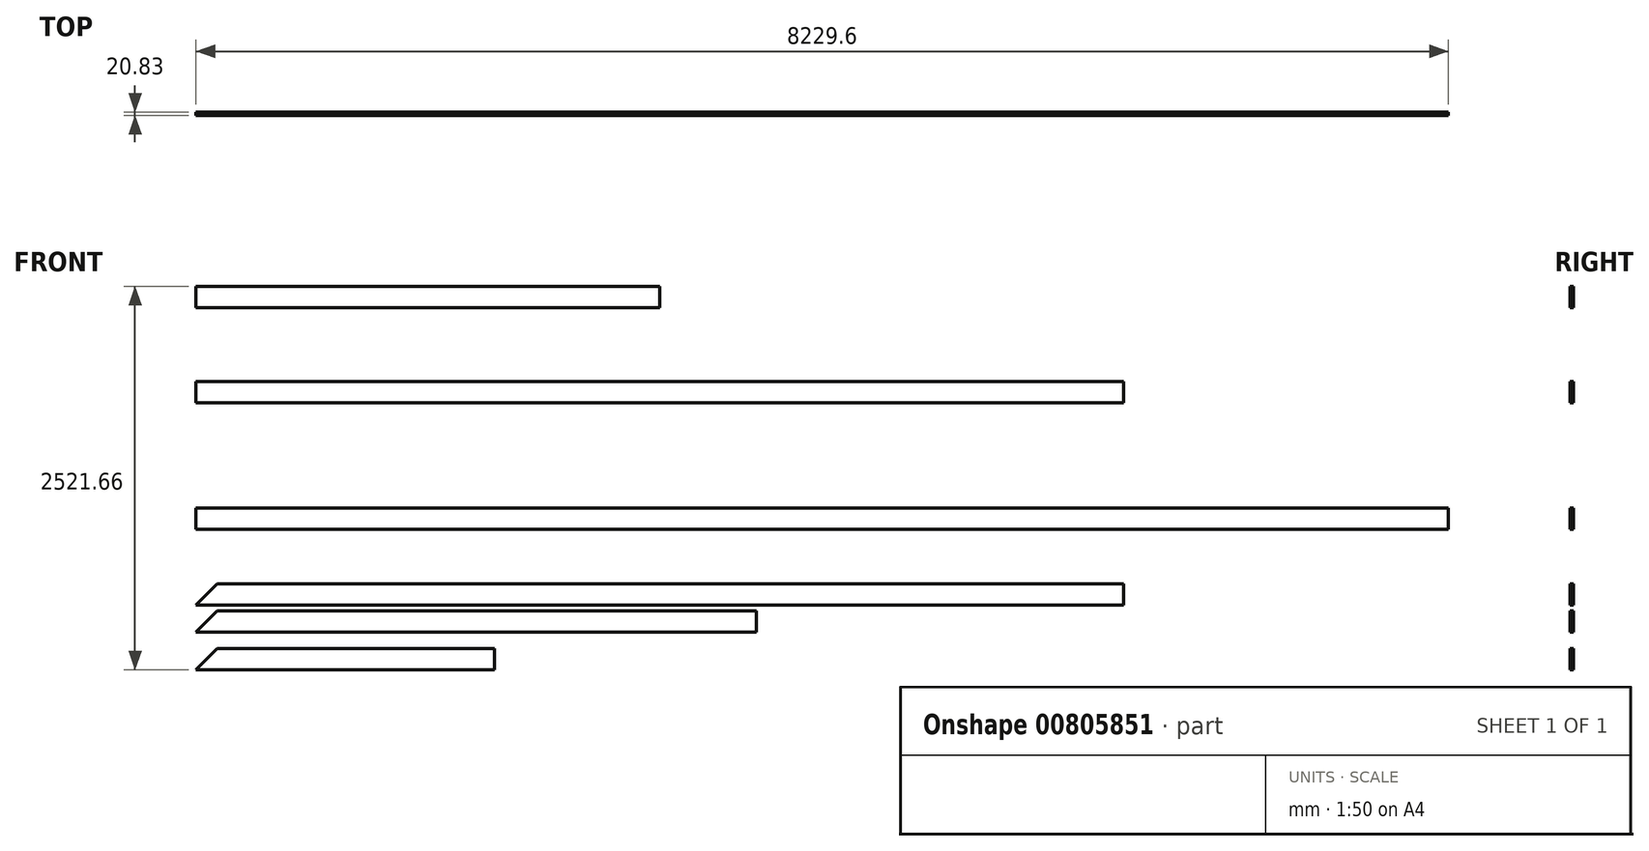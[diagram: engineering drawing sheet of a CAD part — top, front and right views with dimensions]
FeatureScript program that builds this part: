
annotation { "Feature Type Name" : "Feature", "Feature Type Description" : "" }
export const myFeature = defineFeature(function(context is Context, id is Id, definition is map)
    precondition{}
    {
        {
            var Q0;
            Q0=qCreatedBy(makeId("Front.planeOp"),FACE);
            var sketch = newSketch(context, id + "F0", { "sketchPlane" : qUnion([Q0])});
            skLineSegment(sketch, "E0.bottom", {"start": v(6096, 139.7) * mm, "end": v(0, 139.7) * mm});
            skLineSegment(sketch, "E0.top", {"start": v(6096, 0) * mm, "end": v(0, 0) * mm});
            skLineSegment(sketch, "E0.left", {"start": v(6096, 139.7) * mm, "end": v(6096, 0) * mm});
            skLineSegment(sketch, "E0.right", {"start": v(0, 139.7) * mm, "end": v(0, 0) * mm});
            skSolve(sketch);
        }
        {
            var Q0;
            Q0=qSketchRegion(id+"F0",true);
            extrude(context, id + "F1", {"entities" : qUnion([Q0]), "depth" : 20.83 * mm, "offsetDistance" : 25.4 * mm});
        }
        {
            var Q0;
            Q0=qCreatedBy(makeId("Front.planeOp"),FACE);
            var sketch = newSketch(context, id + "F2", { "sketchPlane" : qUnion([Q0])});
            skLineSegment(sketch, "E1.bottom", {"start": v(0, 626.5) * mm, "end": v(3048, 626.5) * mm});
            skLineSegment(sketch, "E1.top", {"start": v(0, 766.2) * mm, "end": v(3048, 766.2) * mm});
            skLineSegment(sketch, "E1.left", {"start": v(0, 626.5) * mm, "end": v(0, 766.2) * mm});
            skLineSegment(sketch, "E1.right", {"start": v(3048, 626.5) * mm, "end": v(3048, 766.2) * mm});
            skSolve(sketch);
        }
        {
            var Q0;
            Q0 = qSketchRegion(id + "F2", true);
            extrude(context, id + "F3", {"entities" : qUnion([Q0]), "depth" : 20.83 * mm, "offsetDistance" : 25.4 * mm});
        }
        {
            var Q0;
            Q0=qCreatedBy(makeId("Front.planeOp"),FACE);
            var sketch = newSketch(context, id + "F4", { "sketchPlane" : qUnion([Q0])});
            skLineSegment(sketch, "E2.bottom", {"start": v(0, -690.7) * mm, "end": v(8229.6, -690.7) * mm});
            skLineSegment(sketch, "E2.top", {"start": v(0, -830.4) * mm, "end": v(8229.6, -830.4) * mm});
            skLineSegment(sketch, "E2.left", {"start": v(0, -690.7) * mm, "end": v(0, -830.4) * mm});
            skLineSegment(sketch, "E2.right", {"start": v(8229.6, -690.7) * mm, "end": v(8229.6, -830.4) * mm});
            skSolve(sketch);
        }
        {
            var Q0;
            Q0 = qSketchRegion(id + "F4", true);
            extrude(context, id + "F5", {"entities" : qUnion([Q0]), "depth" : 20.83 * mm, "offsetDistance" : 25.4 * mm});
        }
        {
            var Q0;
            Q0=qCreatedBy(makeId("Front.planeOp"),FACE);
            var sketch = newSketch(context, id + "F6", { "sketchPlane" : qUnion([Q0])});
            skLineSegment(sketch, "E3.bottom", {"start": v(139.7, -1189.37) * mm, "end": v(6096, -1189.37) * mm});
            skLineSegment(sketch, "E3.top", {"start": v(0, -1329.07) * mm, "end": v(6096, -1329.07) * mm});
            skLineSegment(sketch, "E3.right", {"start": v(6096, -1189.37) * mm, "end": v(6096, -1329.07) * mm});
            skLineSegment(sketch, "E4", {"start": v(0, -1329.07) * mm, "end": v(139.7, -1189.37) * mm});
            skPoint(sketch, "E3.left.start.orphan", {"position": v(0, -1189.37) * mm});
            skSolve(sketch);
        }
        {
            var Q0;
            Q0 = qSketchRegion(id + "F6", true);
            extrude(context, id + "F7", {"entities" : qUnion([Q0]), "depth" : 20.83 * mm, "offsetDistance" : 25.4 * mm});
        }
        {
            var Q0;
            Q0=qCreatedBy(makeId("Front.planeOp"),FACE);
            var sketch = newSketch(context, id + "F8", { "sketchPlane" : qUnion([Q0])});
            skLineSegment(sketch, "E5.bottom", {"start": v(139.7, -1615.75) * mm, "end": v(1962.15, -1615.75) * mm});
            skLineSegment(sketch, "E5.top", {"start": v(0, -1755.45) * mm, "end": v(1962.15, -1755.45) * mm});
            skLineSegment(sketch, "E5.right", {"start": v(1962.15, -1615.75) * mm, "end": v(1962.15, -1755.45) * mm});
            skLineSegment(sketch, "E6", {"start": v(0, -1755.45) * mm, "end": v(139.7, -1615.75) * mm});
            skPoint(sketch, "E5.left.start.orphan", {"position": v(0, -1615.75) * mm});
            skSolve(sketch);
        }
        {
            var Q0;
            Q0 = qSketchRegion(id + "F8", true);
            extrude(context, id + "F9", {"entities" : qUnion([Q0]), "depth" : 20.83 * mm, "offsetDistance" : 25.4 * mm});
        }
        {
            var Q0;
            Q0=qCreatedBy(makeId("Front.planeOp"),FACE);
            var sketch = newSketch(context, id + "F10", { "sketchPlane" : qUnion([Q0])});
            skLineSegment(sketch, "E7.bottom", {"start": v(139.7, -1366.48) * mm, "end": v(3683, -1366.48) * mm});
            skLineSegment(sketch, "E7.top", {"start": v(0, -1506.18) * mm, "end": v(3683, -1506.18) * mm});
            skLineSegment(sketch, "E7.right", {"start": v(3683, -1366.48) * mm, "end": v(3683, -1506.18) * mm});
            skLineSegment(sketch, "E8", {"start": v(0, -1506.18) * mm, "end": v(139.7, -1366.48) * mm});
            skPoint(sketch, "E7.left.start.orphan", {"position": v(0, -1366.48) * mm});
            skSolve(sketch);
        }
        {
            var Q0;
            Q0 = qSketchRegion(id + "F10", true);
            extrude(context, id + "F11", {"entities" : qUnion([Q0]), "depth" : 20.83 * mm, "offsetDistance" : 25.4 * mm});
        }
    });
